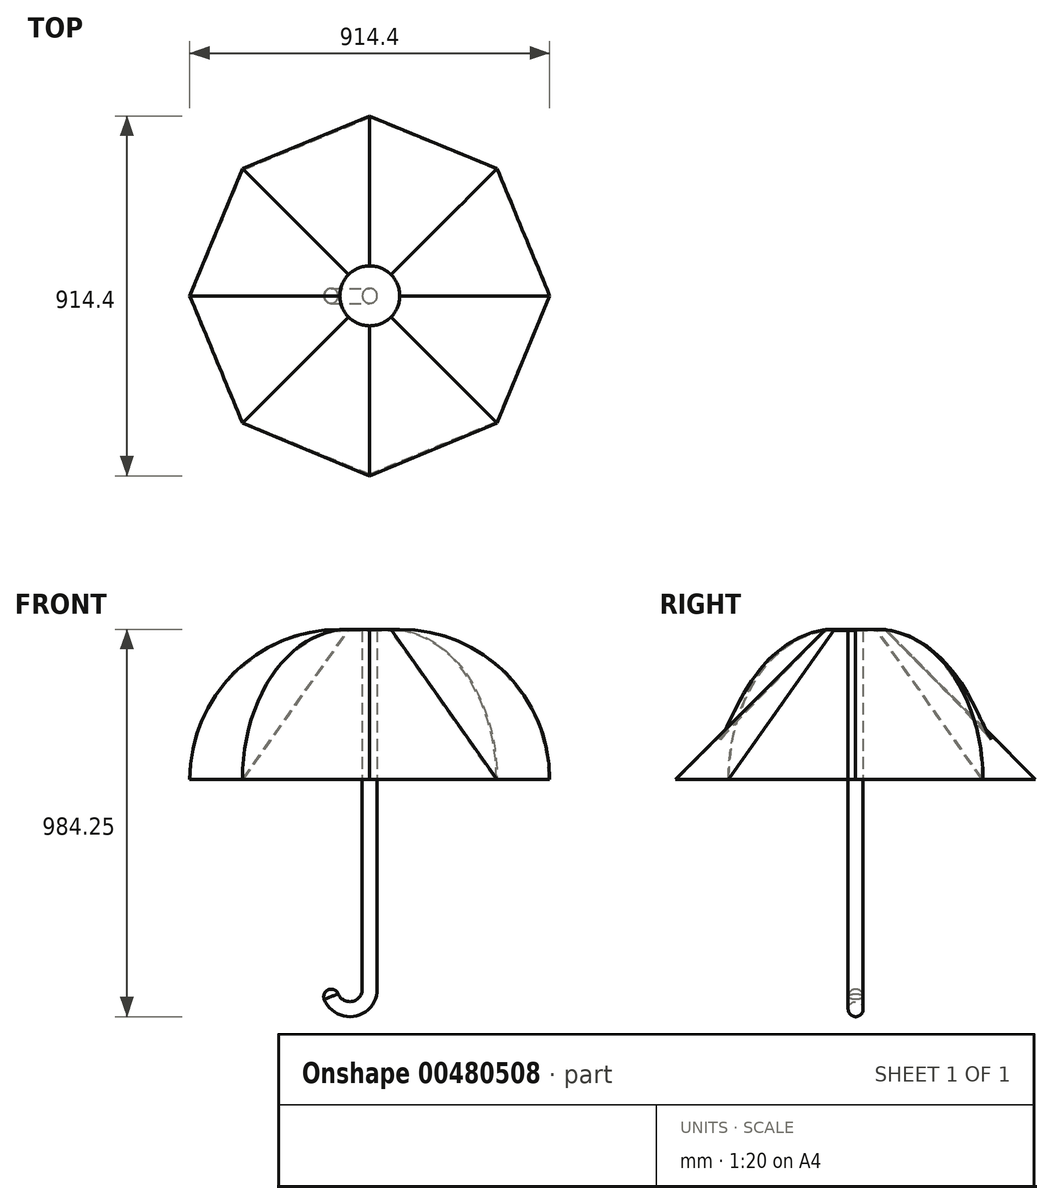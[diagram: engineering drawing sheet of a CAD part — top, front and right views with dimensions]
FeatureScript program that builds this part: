
annotation { "Feature Type Name" : "Feature", "Feature Type Description" : "" }
export const myFeature = defineFeature(function(context is Context, id is Id, definition is map)
    precondition{}
    {
        {
            var Q0;
            Q0=qCreatedBy(makeId("Top.planeOp"),FACE);
            cPlane(context, id + "F0", {"entities" : qUnion([Q0]), "cplaneType" : CPlaneType.OFFSET, "offset" : 381 * mm, "width" : 152.4 * mm, "height" : 152.4 * mm});
        }
        {
            var Q0;
            Q0=qCreatedBy(id+"F0.planeOp",FACE);
            var sketch = newSketch(context, id + "F1", { "sketchPlane" : qUnion([Q0])});
            skCircle(sketch, "E0", {"center": v(0, 0) * mm, "radius": 76.2 * mm});
            skLineSegment(sketch, "E1", {"start": v(0, 76.2) * mm, "end": v(0, -76.2) * mm, "construction": true});
            skLineSegment(sketch, "E2.1.0", {"start": v(53.88, 53.88) * mm, "end": v(-53.88, -53.88) * mm, "construction": true});
            skLineSegment(sketch, "E2.2.0", {"start": v(76.2, 0) * mm, "end": v(-76.2, 0) * mm, "construction": true});
            skLineSegment(sketch, "E2.3.0", {"start": v(53.88, -53.88) * mm, "end": v(-53.88, 53.88) * mm, "construction": true});
            skLineSegment(sketch, "E2.anchor1", {"start": v(0, 0) * mm, "end": v(0, -76.2) * mm, "construction": true});
            skLineSegment(sketch, "E2.anchor2", {"start": v(0, 0) * mm, "end": v(-53.88, 53.88) * mm, "construction": true});
            skSolve(sketch);
        }
        {
            var Q0;
            Q0=qCreatedBy(makeId("Front.planeOp"),FACE);
            var sketch = newSketch(context, id + "F2", { "sketchPlane" : qUnion([Q0])});
            skLineSegment(sketch, "E3", {"start": v(0, 0) * mm, "end": v(0, 381) * mm, "construction": true});
            skSolve(sketch);
        }
        {
            var Q0;
            Q0=qCreatedBy(makeId("Top.planeOp"),FACE);
            var sketch = newSketch(context, id + "F3", { "sketchPlane" : qUnion([Q0])});
            skCircle(sketch, "E4.cCircle", {"center": v(0, 0) * mm, "radius": 422.4 * mm, "construction": true});
            skLineSegment(sketch, "E4.0", {"start": v(323.29, 323.29) * mm, "end": v(457.2, 0) * mm});
            skLineSegment(sketch, "E4.1", {"start": v(457.2, 0) * mm, "end": v(323.29, -323.29) * mm});
            skLineSegment(sketch, "E4.2", {"start": v(323.29, -323.29) * mm, "end": v(0, -457.2) * mm});
            skLineSegment(sketch, "E4.3", {"start": v(0, -457.2) * mm, "end": v(-323.29, -323.29) * mm});
            skLineSegment(sketch, "E4.4", {"start": v(-323.29, -323.29) * mm, "end": v(-457.2, 0) * mm});
            skLineSegment(sketch, "E4.5", {"start": v(-457.2, 0) * mm, "end": v(-323.29, 323.29) * mm});
            skLineSegment(sketch, "E4.6", {"start": v(-323.29, 323.29) * mm, "end": v(0, 457.2) * mm});
            skLineSegment(sketch, "E4.7", {"start": v(0, 457.2) * mm, "end": v(323.29, 323.29) * mm});
            skPoint(sketch, "E4.0.midPoint", {"position": v(390.24, 161.64) * mm});
            skLineSegment(sketch, "E5", {"start": v(0, 457.2) * mm, "end": v(0, -457.2) * mm, "construction": true});
            skSolve(sketch);
        }
        {
            var Q0;
            Q0=qCreatedBy(makeId("Front.planeOp"),FACE);
            var sketch = newSketch(context, id + "F4", { "sketchPlane" : qUnion([Q0])});
            skArc(sketch, "E6", {"start": v(457.2, 0) * mm, "mid": v(345.6, 269.4) * mm, "end": v(76.2, 381) * mm});
            skArc(sketch, "E7.MirrorCS", {"start": v(-457.2, 0) * mm, "mid": v(-345.6, 269.4) * mm, "end": v(-76.2, 381) * mm});
            skSolve(sketch);
        }
        {
            var Q0;
            Q0=qCreatedBy(makeId("Front.planeOp"),FACE);
            var Q1;
            Q1=sQuery(id+"F2.wireOp",EDGE,"E3");
            cPlane(context, id + "F5", {"entities" : qUnion([Q0, Q1]), "cplaneType" : CPlaneType.LINE_ANGLE, "offset" : 25.4 * mm, "angle" : 45 * degree, "width" : 152.4 * mm, "height" : 152.4 * mm});
        }
        {
            var Q0;
            Q0=qCreatedBy(id+"F5.planeOp",FACE);
            var sketch = newSketch(context, id + "F6", { "sketchPlane" : qUnion([Q0])});
            skArc(sketch, "E8", {"start": v(-76.2, 381) * mm, "mid": v(-345.6, 269.4) * mm, "end": v(-457.2, 0) * mm});
            skArc(sketch, "E9.MirrorCS", {"start": v(76.2, 381) * mm, "mid": v(345.6, 269.4) * mm, "end": v(457.2, 0) * mm});
            skSolve(sketch);
        }
        {
            var Q0;
            Q0=qCreatedBy(makeId("Front.planeOp"),FACE);
            var sketch = newSketch(context, id + "F7", { "sketchPlane" : qUnion([Q0])});
            skLineSegment(sketch, "E10", {"start": v(0, 381) * mm, "end": v(0, -533.4) * mm});
            skArc(sketch, "E11", {"start": v(-101.6, -533.4) * mm, "mid": v(-50.8, -584.2) * mm, "end": v(0, -533.4) * mm});
            skSolve(sketch);
        }
        {
            var Q0;
            Q0=qCreatedBy(id+"F0.planeOp",FACE);
            var sketch = newSketch(context, id + "F8", { "sketchPlane" : qUnion([Q0])});
            skCircle(sketch, "E12", {"center": v(0, 0) * mm, "radius": 19.05 * mm});
            skSolve(sketch);
        }
        {
            var Q0;
            Q0=makeQuery(id+"F3.imprint","IMPRINT",FACE,{"disambiguationData":[TD([[makeQuery(id+"F3.imprint","IMPRINT",EDGE,{"derivedFrom":sQuery(id+"F3.wireOp",EDGE,"E4.0")}),-1.0]])]});
            var Q1;
            Q1=makeQuery(id+"F1.imprint","IMPRINT",FACE,{"disambiguationData":[TD([[makeQuery(id+"F1.imprint","IMPRINT",EDGE,{"derivedFrom":sQuery(id+"F1.wireOp",EDGE,"E0")}),1.0]])]});
            var Q2;
            Q2=sQuery(id+"F4.wireOp",EDGE,"E7.MirrorCS");
            var Q3;
            Q3=sQuery(id+"F6.wireOp",EDGE,"E8");
            var Q4;
            Q4=sQuery(id+"F4.wireOp",EDGE,"E6");
            var Q5;
            Q5=sQuery(id+"FwEUsNg9eqqxYRy_0.1.F6.wireOp",EDGE,"E9.MirrorCS");
            var Q6;
            Q6=sQuery(id+"FwEUsNg9eqqxYRy_0.1.F4.wireOp",EDGE,"E7.MirrorCS");
            var Q7;
            Q7=sQuery(id+"F6.wireOp",EDGE,"E9.MirrorCS");
            var Q8;
            Q8=sQuery(id+"FwEUsNg9eqqxYRy_0.1.F6.wireOp",EDGE,"E8");
            var Q9;
            Q9=sQuery(id+"FwEUsNg9eqqxYRy_0.1.F4.wireOp",EDGE,"E6");
            loft(context, id + "F9", {"addGuides" : true, "sheetProfilesArray" : [{ "sheetProfileEntities" : qUnion([Q0]) }, { "sheetProfileEntities" : qUnion([Q1]) }], "guidesArray" : [{ "guideEntities" : qUnion([Q2]), "guideDerivativeType" : LoftGuideDerivativeType.DEFAULT, "guideDerivativeMagnitude" : 1 }, { "guideEntities" : qUnion([Q3]), "guideDerivativeType" : LoftGuideDerivativeType.DEFAULT, "guideDerivativeMagnitude" : 1 }, { "guideEntities" : qUnion([Q4]), "guideDerivativeType" : LoftGuideDerivativeType.DEFAULT, "guideDerivativeMagnitude" : 1 }, { "guideEntities" : qUnion([Q5]), "guideDerivativeType" : LoftGuideDerivativeType.DEFAULT, "guideDerivativeMagnitude" : 1 }, { "guideEntities" : qUnion([Q6]), "guideDerivativeType" : LoftGuideDerivativeType.DEFAULT, "guideDerivativeMagnitude" : 1 }, { "guideEntities" : qUnion([Q7]), "guideDerivativeType" : LoftGuideDerivativeType.DEFAULT, "guideDerivativeMagnitude" : 1 }, { "guideEntities" : qUnion([Q8]), "guideDerivativeType" : LoftGuideDerivativeType.DEFAULT, "guideDerivativeMagnitude" : 1 }, { "guideEntities" : qUnion([Q9]), "guideDerivativeType" : LoftGuideDerivativeType.DEFAULT, "guideDerivativeMagnitude" : 1 }]});
        }
        {
            var Q0;
            Q0=makeQuery(id+"F9.opLoft","CAP_FACE",FACE,{"disambiguationData":[OSD([makeQuery(id+"F3.imprint","IMPRINT",FACE,{"disambiguationData":[TD([[makeQuery(id+"F3.imprint","IMPRINT",EDGE,{"derivedFrom":sQuery(id+"F3.wireOp",EDGE,"E4.0")}),-1.0]])]})])],"isStart":true});
            shell(context, id + "F10", {"entities" : qUnion([Q0]), "thickness" : 2.54 * mm});
        }
        {
            var Q0;
            Q0=makeQuery(id+"F8.imprint","IMPRINT",FACE,{"disambiguationData":[TD([[makeQuery(id+"F8.imprint","IMPRINT",EDGE,{"derivedFrom":sQuery(id+"F8.wireOp",EDGE,"E12")}),1.0]])]});
            var Q1;
            Q1=sQuery(id+"F7.wireOp",EDGE,"E10");
            var Q2;
            Q2=sQuery(id+"F7.wireOp",EDGE,"E11");
            sweep(context, id + "F11", {"operationType" : NewBodyOperationType.ADD, "profiles" : qUnion([Q0]), "path" : qUnion([Q1, Q2])});
        }
        {
            var Q0;
            Q0=makeQuery(id+"F11.opSweep","CAP_EDGE",EDGE,{"disambiguationData":[OSD([sQuery(id+"F7.wireOp",VERTEX,"E11.start"),sQuery(id+"F8.wireOp",EDGE,"E12")])],"isStart":false});
            fillet(context, id + "F12", {"entities" : qUnion([Q0]), "radius" : 19.05 * mm, "tangentPropagation" : true, "allowEdgeOverflow" : false});
        }
    });
